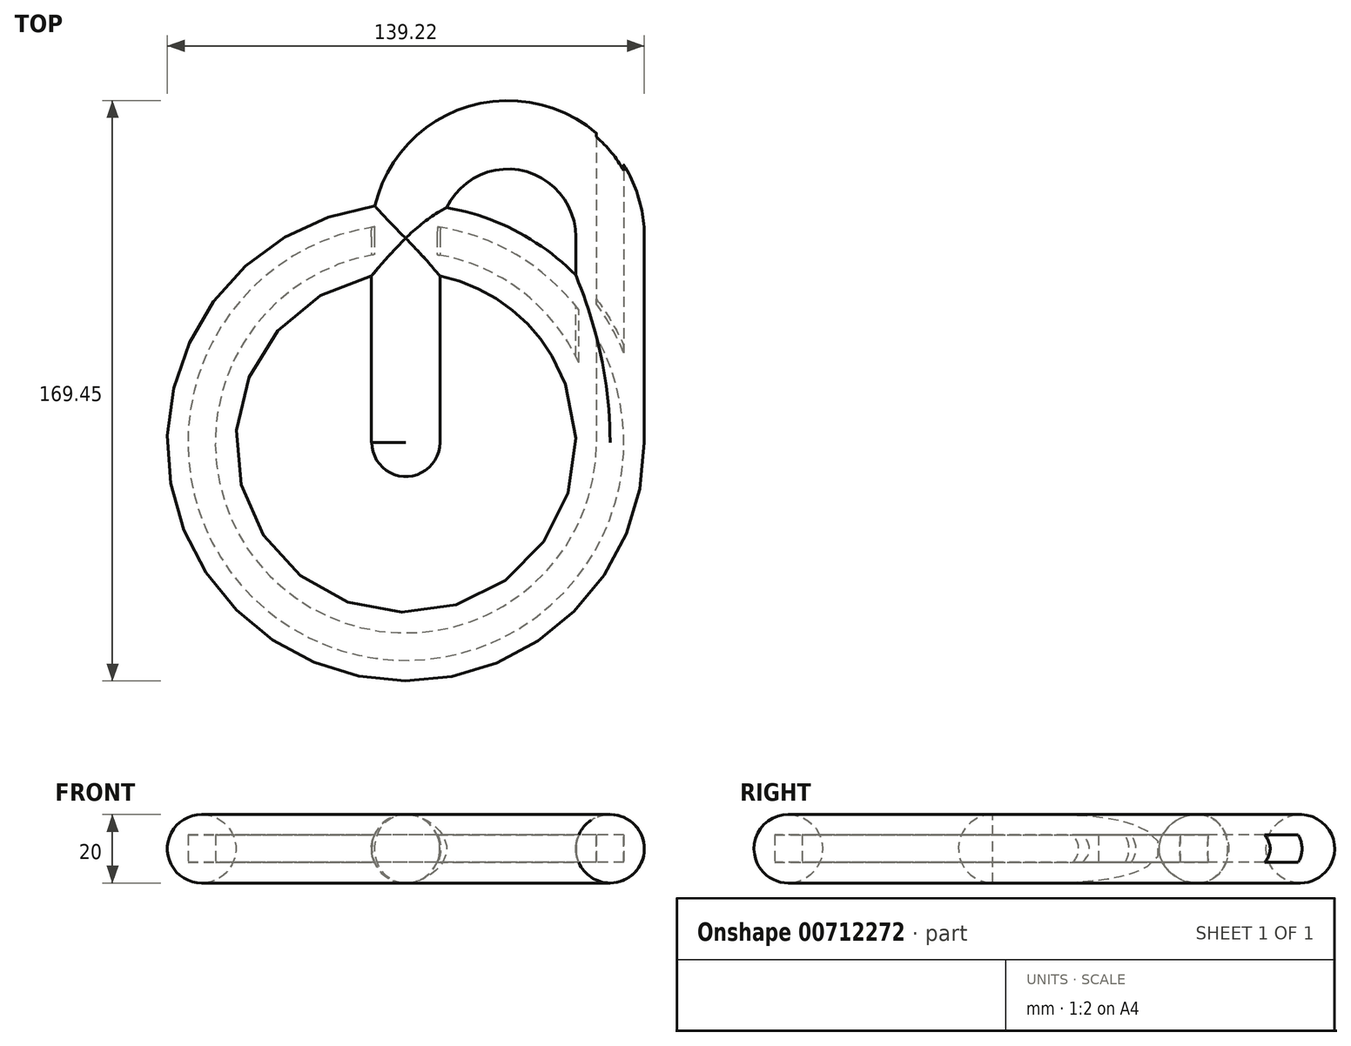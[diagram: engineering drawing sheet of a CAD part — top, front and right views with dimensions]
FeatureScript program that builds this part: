
annotation { "Feature Type Name" : "Feature", "Feature Type Description" : "" }
export const myFeature = defineFeature(function(context is Context, id is Id, definition is map)
    precondition{}
    {
        {
            var Q0;
            Q0=qCreatedBy(makeId("Top.planeOp"),FACE);
            var sketch = newSketch(context, id + "F0", { "sketchPlane" : qUnion([Q0])});
            skArc(sketch, "E0", {"start": v(30, 0) * mm, "mid": v(0, 30) * mm, "end": v(-30, 0) * mm});
            skLineSegment(sketch, "E1", {"start": v(-30, 0) * mm, "end": v(-30, -60) * mm});
            skLineSegment(sketch, "E2", {"start": v(30, 0) * mm, "end": v(30, -60) * mm});
            skSolve(sketch);
        }
        {
            var Q0;
            Q0=qCreatedBy(makeId("Front.planeOp"),FACE);
            cPlane(context, id + "F1", {"entities" : qUnion([Q0]), "cplaneType" : CPlaneType.OFFSET, "offset" : 60 * mm, "width" : 150 * mm, "height" : 150 * mm});
        }
        {
            var Q0;
            Q0=qCreatedBy(id+"F1.planeOp",FACE);
            var sketch = newSketch(context, id + "F2", { "sketchPlane" : qUnion([Q0])});
            skCircle(sketch, "E3", {"center": v(29.84, 0) * mm, "radius": 10 * mm});
            skSolve(sketch);
        }
        {
            var Q0;
            Q0=makeQuery(id+"F2.imprint","IMPRINT",FACE,{"disambiguationData":[TD([[makeQuery(id+"F2.imprint","IMPRINT",EDGE,{"derivedFrom":sQuery(id+"F2.wireOp",EDGE,"E3")}),1.0]])]});
            var Q1;
            Q1=sQuery(id+"F0.wireOp",EDGE,"E2");
            var Q2;
            Q2=sQuery(id+"F0.wireOp",EDGE,"E0");
            var Q3;
            Q3=sQuery(id+"F0.wireOp",EDGE,"E1");
            sweep(context, id + "F3", {"profiles" : qUnion([Q0]), "path" : qUnion([Q1, Q2, Q3])});
        }
        {
            var Q0;
            Q0=makeQuery(id+"F3.opSweep","CAP_FACE",FACE,{"disambiguationData":[OSD([sQuery(id+"F0.wireOp",VERTEX,"E2.end"),sQuery(id+"F2.wireOp",EDGE,"E3")])],"isStart":true});
            var sketch = newSketch(context, id + "F4", { "sketchPlane" : qUnion([Q0])});
            skLineSegment(sketch, "E4", {"start": v(19.84, 0) * mm, "end": v(39.84, 0) * mm});
            skLineSegment(sketch, "E5.bottom", {"start": v(33.84, 4) * mm, "end": v(25.84, 4) * mm});
            skLineSegment(sketch, "E5.top", {"start": v(33.84, -4) * mm, "end": v(25.84, -4) * mm});
            skLineSegment(sketch, "E5.left", {"start": v(33.84, 4) * mm, "end": v(33.84, -4) * mm});
            skLineSegment(sketch, "E5.right", {"start": v(25.84, 4) * mm, "end": v(25.84, -4) * mm});
            skPoint(sketch, "E5.middle", {"position": v(29.84, 0) * mm});
            skSolve(sketch);
        }
        {
            var Q0;
            Q0=makeQuery(id+"F3.opSweep","CAP_FACE",FACE,{"disambiguationData":[OSD([sQuery(id+"F0.wireOp",VERTEX,"E1.end"),sQuery(id+"F2.wireOp",EDGE,"E3")])],"isStart":false});
            var sketch = newSketch(context, id + "F5", { "sketchPlane" : qUnion([Q0])});
            skLineSegment(sketch, "E6", {"start": v(-29.77, 10) * mm, "end": v(-29.77, -10) * mm});
            skSolve(sketch);
        }
        {
            var Q0;
            {var subQ5=sQuery(id+"F4.wireOp",EDGE,"E5.bottom");Q0=makeQuery(id+"F4.imprint","IMPRINT",FACE,{"disambiguationData":[TD([[makeQuery(id+"F4.imprint","IMPRINT",EDGE,{"derivedFrom":subQ5}),1.0]])]});}
            var Q1;
            {var subQ5=sQuery(id+"F4.wireOp",EDGE,"E5.top");Q1=makeQuery(id+"F4.imprint","IMPRINT",FACE,{"disambiguationData":[TD([[makeQuery(id+"F4.imprint","IMPRINT",EDGE,{"derivedFrom":subQ5}),-1.0]])]});}
            extrude(context, id + "F6", {"entities" : qUnion([Q0, Q1]), "operationType" : NewBodyOperationType.REMOVE, "endBound" : BoundingType.THROUGH_ALL, "oppositeDirection" : true, "depth" : 50 * mm, "offsetDistance" : 25 * mm});
        }
        {
            var Q0;
            {var subQ0=sQuery(id+"F5.wireOp",EDGE,"E6");Q0=makeQuery(id+"F5.imprint","IMPRINT",FACE,{"disambiguationData":[TD([[makeQuery(id+"F5.imprint","IMPRINT",EDGE,{"derivedFrom":subQ0}),1.0]])]});}
            var Q1;
            Q1=sQuery(id+"F5.wireOp",EDGE,"E6");
            revolve(context, id + "F7", {"operationType" : NewBodyOperationType.ADD, "surfaceOperationType" : NewSurfaceOperationType.NEW, "entities" : qUnion([Q0]), "axis" : qUnion([Q1]), "revolveType" : RevolveType.FULL});
        }
        {
            var Q0;
            Q0=makeQuery(id+"F3.opSweep","CAP_FACE",FACE,{"disambiguationData":[OSD([sQuery(id+"F0.wireOp",VERTEX,"E2.end"),sQuery(id+"F2.wireOp",EDGE,"E3")])],"isStart":true});
            var Q1;
            Q1=makeQuery(id+"F7.opRevolve","SWEPT_FACE",FACE,{"disambiguationData":[OSD([sQuery(id+"F0.wireOp",VERTEX,"E1.end"),sQuery(id+"F2.wireOp",EDGE,"E3")])]});
            revolve(context, id + "F8", {"operationType" : NewBodyOperationType.ADD, "surfaceOperationType" : NewSurfaceOperationType.NEW, "entities" : qUnion([Q0]), "axis" : qUnion([Q1]), "revolveType" : RevolveType.FULL});
        }
    });
